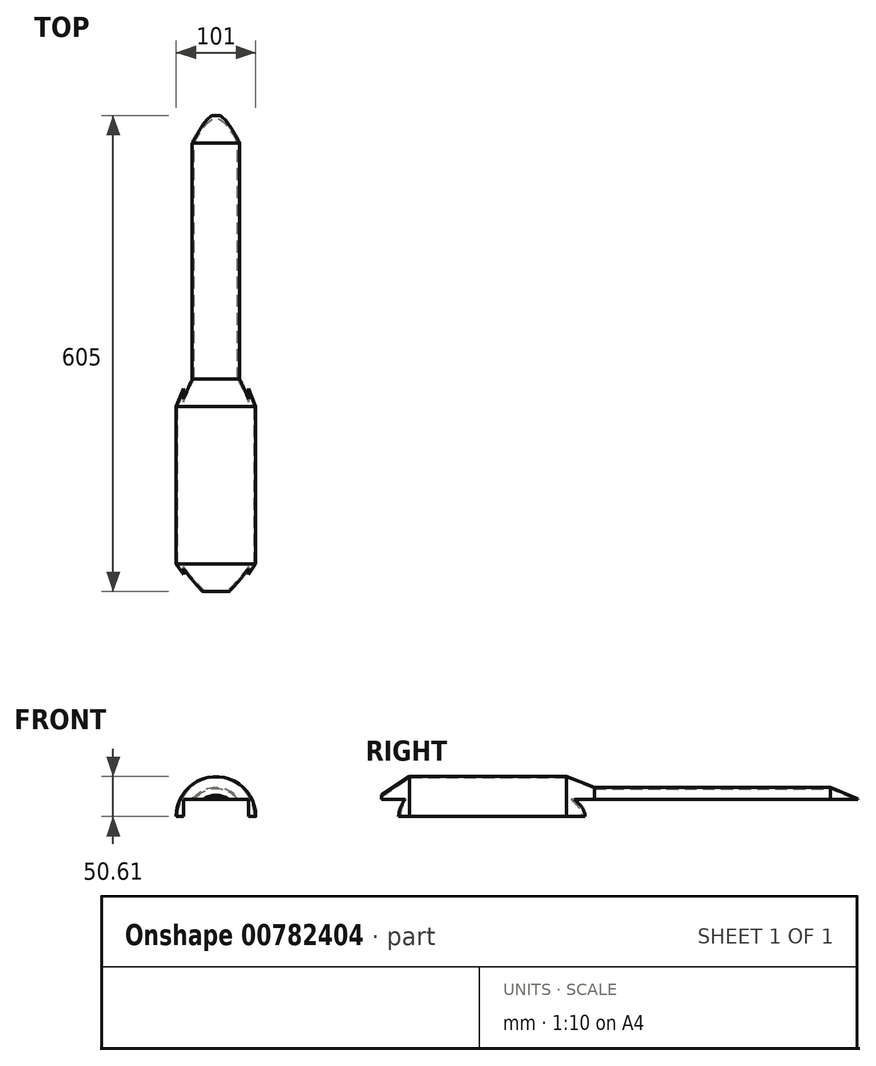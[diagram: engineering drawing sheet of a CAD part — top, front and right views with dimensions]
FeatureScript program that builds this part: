
annotation { "Feature Type Name" : "Feature", "Feature Type Description" : "" }
export const myFeature = defineFeature(function(context is Context, id is Id, definition is map)
    precondition{}
    {
        {
            assignVariable(context, id + "F0", {"name" : "FPDIST", "anyValue" : 35});
        }
        {
            assignVariable(context, id + "F1", {"name" : "ELECTDIST", "anyValue" : 200});
        }
        {
            assignVariable(context, id + "F2", {"name" : "SSDIST", "anyValue" : 35});
        }
        {
            assignVariable(context, id + "F3", {"name" : "SEDIST", "anyValue" : 300});
        }
        {
            assignVariable(context, id + "F4", {"name" : "RPDIST", "anyValue" : 35});
        }
        {
            var Q0;
            Q0=qCreatedBy(makeId("Front.planeOp"),FACE);
            var sketch = newSketch(context, id + "F5", { "sketchPlane" : qUnion([Q0])});
            skCircle(sketch, "E0", {"center": v(0, 0) * mm, "radius": 50.5 * mm});
            skCircle(sketch, "E1", {"center": v(0, 0) * mm, "radius": 49 * mm});
            skLineSegment(sketch, "E2", {"start": v(-50.5, 0) * mm, "end": v(-49, 0) * mm});
            skLineSegment(sketch, "E3", {"start": v(49, 0) * mm, "end": v(50.5, 0) * mm});
            skSolve(sketch);
        }
        {
            var Q0;
            Q0=qCreatedBy(makeId("Front.planeOp"),FACE);
            cPlane(context, id + "F6", {"entities" : qUnion([Q0]), "cplaneType" : CPlaneType.OFFSET, "offset" : (getVariable(context, 'FPDIST')) * mm, "width" : 150 * mm, "height" : 150 * mm});
        }
        {
            var Q0;
            Q0=qCreatedBy(makeId("Front.planeOp"),FACE);
            cPlane(context, id + "F7", {"entities" : qUnion([Q0]), "cplaneType" : CPlaneType.OFFSET, "offset" : (getVariable(context, 'ELECTDIST')) * mm, "oppositeDirection" : true, "width" : 150 * mm, "height" : 150 * mm});
        }
        {
            var Q0;
            Q0=qCreatedBy(id+"F7.planeOp",FACE);
            cPlane(context, id + "F8", {"entities" : qUnion([Q0]), "cplaneType" : CPlaneType.OFFSET, "offset" : (getVariable(context, 'SSDIST')) * mm, "oppositeDirection" : true, "width" : 150 * mm, "height" : 150 * mm});
        }
        {
            var Q0;
            Q0=qCreatedBy(id+"F8.planeOp",FACE);
            cPlane(context, id + "F9", {"entities" : qUnion([Q0]), "cplaneType" : CPlaneType.OFFSET, "offset" : (getVariable(context, 'SEDIST')) * mm, "oppositeDirection" : true, "width" : 150 * mm, "height" : 150 * mm});
        }
        {
            var Q0;
            Q0=qCreatedBy(id+"F9.planeOp",FACE);
            cPlane(context, id + "F10", {"entities" : qUnion([Q0]), "cplaneType" : CPlaneType.OFFSET, "offset" : (getVariable(context, 'RPDIST')) * mm, "oppositeDirection" : true, "width" : 150 * mm, "height" : 150 * mm});
        }
        {
            var Q0;
            Q0=qCreatedBy(id+"F6.planeOp",FACE);
            var sketch = newSketch(context, id + "F11", { "sketchPlane" : qUnion([Q0])});
            skCircle(sketch, "E4", {"center": v(0, 0) * mm, "radius": 27 * mm});
            skCircle(sketch, "E5", {"center": v(0, 0) * mm, "radius": 25 * mm});
            skLineSegment(sketch, "E6", {"start": v(-27, 0) * mm, "end": v(-25, 0) * mm});
            skLineSegment(sketch, "E7", {"start": v(25, -0.02) * mm, "end": v(27, -0.02) * mm});
            skSolve(sketch);
        }
        {
            var Q0;
            Q0=qCreatedBy(id+"F7.planeOp",FACE);
            var sketch = newSketch(context, id + "F12", { "sketchPlane" : qUnion([Q0])});
            skCircle(sketch, "E8", {"center": v(0, 0) * mm, "radius": 50.5 * mm});
            skCircle(sketch, "E9", {"center": v(0, 0) * mm, "radius": 49 * mm});
            skLineSegment(sketch, "E10", {"start": v(-50.5, -0.11) * mm, "end": v(-49, -0.11) * mm});
            skLineSegment(sketch, "E11", {"start": v(49, -0.11) * mm, "end": v(50.5, -0.11) * mm});
            skSolve(sketch);
        }
        {
            var Q0;
            Q0=qCreatedBy(id+"F8.planeOp",FACE);
            var sketch = newSketch(context, id + "F13", { "sketchPlane" : qUnion([Q0])});
            skCircle(sketch, "E12", {"center": v(0, 0) * mm, "radius": 37 * mm});
            skCircle(sketch, "E13", {"center": v(0, 0) * mm, "radius": 35 * mm});
            skLineSegment(sketch, "E14", {"start": v(-37, 0) * mm, "end": v(-35, 0) * mm});
            skLineSegment(sketch, "E15", {"start": v(35, 0) * mm, "end": v(37, 0) * mm});
            skSolve(sketch);
        }
        {
            var Q0;
            Q0=qCreatedBy(id+"F9.planeOp",FACE);
            var sketch = newSketch(context, id + "F14", { "sketchPlane" : qUnion([Q0])});
            skCircle(sketch, "E16", {"center": v(0, 0) * mm, "radius": 37 * mm});
            skCircle(sketch, "E17", {"center": v(0, 0) * mm, "radius": 35 * mm});
            skLineSegment(sketch, "E18", {"start": v(-37, 0.13) * mm, "end": v(-35, 0.13) * mm});
            skLineSegment(sketch, "E19", {"start": v(35, 0.13) * mm, "end": v(37, 0.13) * mm});
            skSolve(sketch);
        }
        {
            var Q0;
            Q0=qCreatedBy(id+"F10.planeOp",FACE);
            var sketch = newSketch(context, id + "F15", { "sketchPlane" : qUnion([Q0])});
            skCircle(sketch, "E20", {"center": v(0, 0) * mm, "radius": 22 * mm});
            skCircle(sketch, "E21", {"center": v(0, 0) * mm, "radius": 20 * mm});
            skLineSegment(sketch, "E22", {"start": v(-22, 0.02) * mm, "end": v(-20, 0.02) * mm});
            skLineSegment(sketch, "E23", {"start": v(20, 0.02) * mm, "end": v(22, 0.02) * mm});
            skSolve(sketch);
        }
        {
            var Q0;
            {var subQ0=sQuery(id+"F11.wireOp",EDGE,"E6");Q0=makeQuery(id+"F11.imprint","IMPRINT",FACE,{"disambiguationData":[TD([[makeQuery(id+"F11.imprint","IMPRINT",EDGE,{"derivedFrom":subQ0}),1.0]])]});}
            var Q1;
            {var subQ0=sQuery(id+"F5.wireOp",EDGE,"E2");Q1=makeQuery(id+"F5.imprint","IMPRINT",FACE,{"disambiguationData":[TD([[makeQuery(id+"F5.imprint","IMPRINT",EDGE,{"derivedFrom":subQ0}),1.0]])]});}
            var Q2;
            Q2=sQuery(id+"FQz9rfOLmXyHpMg_0.wireOp",EDGE,"uAbCC71v-ZNXH-bkIy-RPOa-loDlzJmMccou");
            var Q3;
            Q3=sQuery(id+"FQz9rfOLmXyHpMg_0.wireOp",EDGE,"BHh4PDZl-9Qbo-o1Od-lUql-6WkpFpjAwwEc");
            var Q4;
            Q4=sQuery(id+"FQz9rfOLmXyHpMg_0.wireOp",EDGE,"oVwYHCgB-pV1k-eqX5-T6Y1-jWb26eQNFG5w");
            var Q5;
            Q5=sQuery(id+"FQz9rfOLmXyHpMg_0.wireOp",EDGE,"rKKV9NwO-jNbV-mexz-2yBo-cgzd4MubIoCG");
            var Q6;
            Q6=sQuery(id+"FQz9rfOLmXyHpMg_0.wireOp",EDGE,"x7hHLVG2-yGW5-iGfC-CHEE-JPPsx5alTI5c");
            loft(context, id + "F16", {"sheetProfilesArray" : [{ "sheetProfileEntities" : qUnion([Q0]) }, { "sheetProfileEntities" : qUnion([Q1]) }], "guidesArray" : [{ "guideEntities" : qUnion([Q2]), "guideDerivativeType" : LoftGuideDerivativeType.DEFAULT, "guideDerivativeMagnitude" : 1 }, { "guideEntities" : qUnion([Q3]), "guideDerivativeType" : LoftGuideDerivativeType.DEFAULT, "guideDerivativeMagnitude" : 1 }, { "guideEntities" : qUnion([Q4]), "guideDerivativeType" : LoftGuideDerivativeType.DEFAULT, "guideDerivativeMagnitude" : 1 }, { "guideEntities" : qUnion([Q5]), "guideDerivativeType" : LoftGuideDerivativeType.DEFAULT, "guideDerivativeMagnitude" : 1 }, { "guideEntities" : qUnion([Q6]), "guideDerivativeType" : LoftGuideDerivativeType.DEFAULT, "guideDerivativeMagnitude" : 1 }]});
        }
        {
            var Q1;
            {var subQ0=sQuery(id+"F5.wireOp",EDGE,"E2");Q1=makeQuery(id+"F16.opLoft","CAP_FACE",FACE,{"disambiguationData":[OSD([makeQuery(id+"F5.imprint","IMPRINT",FACE,{"disambiguationData":[TD([[makeQuery(id+"F5.imprint","IMPRINT",EDGE,{"derivedFrom":subQ0}),1.0]])]})])],"isStart":true});}
            var Q2;
            {var subQ0=sQuery(id+"F12.wireOp",EDGE,"E10");Q2=makeQuery(id+"F12.imprint","IMPRINT",FACE,{"disambiguationData":[TD([[makeQuery(id+"F12.imprint","IMPRINT",EDGE,{"derivedFrom":subQ0}),1.0]])]});}
            loft(context, id + "F17", {"operationType" : NewBodyOperationType.ADD, "sheetProfilesArray" : [{ "sheetProfileEntities" : qUnion([Q1]) }, { "sheetProfileEntities" : qUnion([Q2]) }]});
        }
        {
            var Q1;
            {var subQ0=sQuery(id+"F12.wireOp",EDGE,"E10");Q1=makeQuery(id+"F17.opLoft","CAP_FACE",FACE,{"disambiguationData":[OSD([makeQuery(id+"F12.imprint","IMPRINT",FACE,{"disambiguationData":[TD([[makeQuery(id+"F12.imprint","IMPRINT",EDGE,{"derivedFrom":subQ0}),1.0]])]})])],"isStart":true});}
            var Q2;
            {var subQ0=sQuery(id+"F13.wireOp",EDGE,"E14");Q2=makeQuery(id+"F13.imprint","IMPRINT",FACE,{"disambiguationData":[TD([[makeQuery(id+"F13.imprint","IMPRINT",EDGE,{"derivedFrom":subQ0}),1.0]])]});}
            loft(context, id + "F18", {"operationType" : NewBodyOperationType.ADD, "sheetProfilesArray" : [{ "sheetProfileEntities" : qUnion([Q1]) }, { "sheetProfileEntities" : qUnion([Q2]) }]});
        }
        {
            var Q1;
            {var subQ0=sQuery(id+"F13.wireOp",EDGE,"E14");Q1=makeQuery(id+"F18.opLoft","CAP_FACE",FACE,{"disambiguationData":[OSD([makeQuery(id+"F13.imprint","IMPRINT",FACE,{"disambiguationData":[TD([[makeQuery(id+"F13.imprint","IMPRINT",EDGE,{"derivedFrom":subQ0}),1.0]])]})])],"isStart":true});}
            var Q2;
            {var subQ0=sQuery(id+"F14.wireOp",EDGE,"E18");Q2=makeQuery(id+"F14.imprint","IMPRINT",FACE,{"disambiguationData":[TD([[makeQuery(id+"F14.imprint","IMPRINT",EDGE,{"derivedFrom":subQ0}),1.0]])]});}
            loft(context, id + "F19", {"operationType" : NewBodyOperationType.ADD, "sheetProfilesArray" : [{ "sheetProfileEntities" : qUnion([Q1]) }, { "sheetProfileEntities" : qUnion([Q2]) }]});
        }
        {
            var Q1;
            {var subQ0=sQuery(id+"F14.wireOp",EDGE,"E18");Q1=makeQuery(id+"F19.opLoft","CAP_FACE",FACE,{"disambiguationData":[OSD([makeQuery(id+"F14.imprint","IMPRINT",FACE,{"disambiguationData":[TD([[makeQuery(id+"F14.imprint","IMPRINT",EDGE,{"derivedFrom":subQ0}),1.0]])]})])],"isStart":true});}
            var Q2;
            {var subQ0=sQuery(id+"F15.wireOp",EDGE,"E22");Q2=makeQuery(id+"F15.imprint","IMPRINT",FACE,{"disambiguationData":[TD([[makeQuery(id+"F15.imprint","IMPRINT",EDGE,{"derivedFrom":subQ0}),1.0]])]});}
            loft(context, id + "F20", {"operationType" : NewBodyOperationType.ADD, "sheetProfilesArray" : [{ "sheetProfileEntities" : qUnion([Q1]) }, { "sheetProfileEntities" : qUnion([Q2]) }]});
        }
        {
            var Q0;
            Q0=qCreatedBy(id+"F6.planeOp",FACE);
            var sketch = newSketch(context, id + "F21", { "sketchPlane" : qUnion([Q0])});
            skLineSegment(sketch, "E24.bottom", {"start": v(-41.5, 21.5) * mm, "end": v(41.5, 21.5) * mm});
            skLineSegment(sketch, "E24.top", {"start": v(-41.5, -21.5) * mm, "end": v(41.5, -21.5) * mm});
            skLineSegment(sketch, "E24.left", {"start": v(-41.5, 21.5) * mm, "end": v(-41.5, -21.5) * mm});
            skLineSegment(sketch, "E24.right", {"start": v(41.5, 21.5) * mm, "end": v(41.5, -21.5) * mm});
            skPoint(sketch, "E24.middle", {"position": v(0, 0) * mm});
            skSolve(sketch);
        }
        {
            var Q0;
            Q0=makeQuery(id+"F21.imprint","IMPRINT",FACE,{"disambiguationData":[TD([[makeQuery(id+"F21.imprint","IMPRINT",EDGE,{"derivedFrom":sQuery(id+"F21.wireOp",EDGE,"E24.bottom")}),-1.0]])]});
            extrude(context, id + "F22", {"entities" : qUnion([Q0]), "operationType" : NewBodyOperationType.REMOVE, "endBound" : BoundingType.THROUGH_ALL, "oppositeDirection" : true, "depth" : 25 * mm, "offsetDistance" : 25 * mm});
        }
    });
